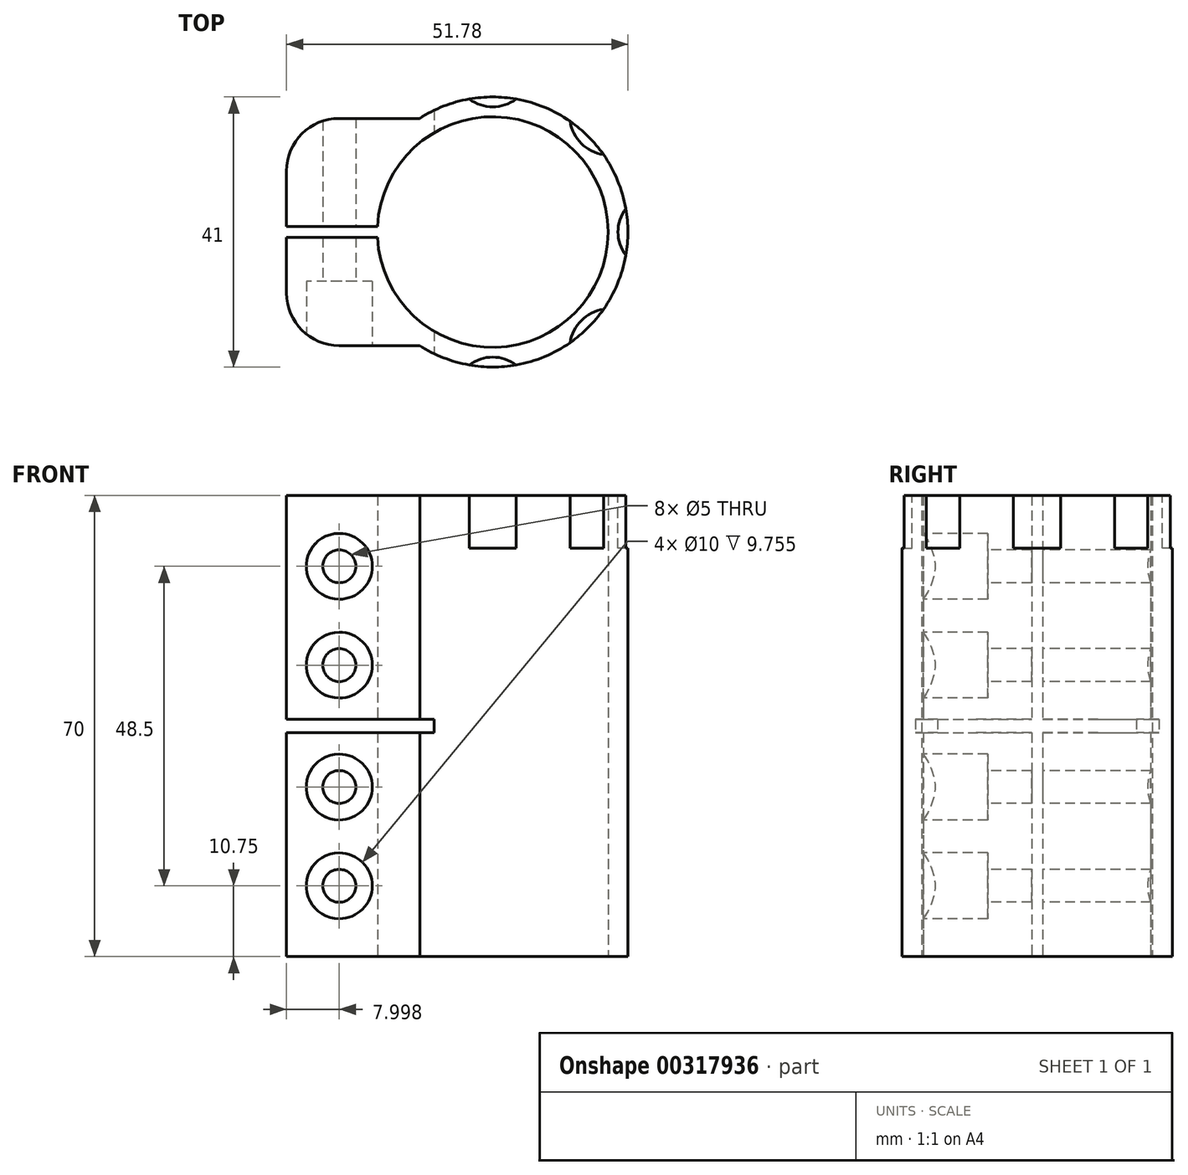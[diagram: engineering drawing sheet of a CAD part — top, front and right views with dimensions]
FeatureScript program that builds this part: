
annotation { "Feature Type Name" : "Feature", "Feature Type Description" : "" }
export const myFeature = defineFeature(function(context is Context, id is Id, definition is map)
    precondition{}
    {
        {
            var Q0;
            Q0=qCreatedBy(makeId("Top.planeOp"),FACE);
            var sketch = newSketch(context, id + "F0", { "sketchPlane" : qUnion([Q0])});
            skArc(sketch, "E0", {"start": v(-17.48, -0.85) * mm, "mid": v(17.5, 0) * mm, "end": v(-17.48, 0.85) * mm});
            skArc(sketch, "E1", {"start": v(-11.08, -17.25) * mm, "mid": v(20.5, 0) * mm, "end": v(-11.08, 17.25) * mm});
            skLineSegment(sketch, "E2", {"start": v(-11.08, 17.25) * mm, "end": v(-23.28, 17.25) * mm});
            skLineSegment(sketch, "E3", {"start": v(-31.28, 9.25) * mm, "end": v(-31.28, 0.85) * mm});
            skLineSegment(sketch, "E4", {"start": v(-31.28, 0.85) * mm, "end": v(-20.48, 0.85) * mm});
            skPoint(sketch, "E5.visualSharp", {"position": v(-31.28, 17.25) * mm});
            skArc(sketch, "E5.filletArc", {"start": v(-23.28, 17.25) * mm, "mid": v(-28.94, 14.9) * mm, "end": v(-31.28, 9.25) * mm});
            skLineSegment(sketch, "E6", {"start": v(0, 0) * mm, "end": v(31.62, 0) * mm, "construction": true});
            skLineSegment(sketch, "E7.MirrorCS", {"start": v(-31.28, -0.85) * mm, "end": v(-20.48, -0.85) * mm});
            skLineSegment(sketch, "E8.MirrorCS", {"start": v(-11.08, -17.25) * mm, "end": v(-23.28, -17.25) * mm});
            skLineSegment(sketch, "E9.MirrorCS", {"start": v(-31.28, -9.25) * mm, "end": v(-31.28, -0.85) * mm});
            skArc(sketch, "E10.MirrorCS", {"start": v(-23.28, -17.25) * mm, "mid": v(-28.94, -14.9) * mm, "end": v(-31.28, -9.25) * mm});
            skLineSegment(sketch, "E11", {"start": v(-20.48, 0.85) * mm, "end": v(-17.48, 0.85) * mm});
            skLineSegment(sketch, "E12", {"start": v(-20.48, -0.85) * mm, "end": v(-17.48, -0.85) * mm});
            skSolve(sketch);
        }
        {
            var Q0;
            Q0=qSketchRegion(id+"F0",true);
            extrude(context, id + "F1", {"entities" : qUnion([Q0]), "endBound" : BoundingType.SYMMETRIC, "depth" : 70 * mm});
        }
        {
            var Q0;
            Q0=makeQuery(id+"F1.opExtrude","SWEPT_FACE",FACE,{"disambiguationData":[OSD([sQuery(id+"F0.wireOp",EDGE,"E8.MirrorCS")])]});
            var sketch = newSketch(context, id + "F2", { "sketchPlane" : qUnion([Q0])});
            skPoint(sketch, "E13", {"position": v(-5.74, 0) * mm});
            skPoint(sketch, "E14", {"position": v(-23.28, -24.25) * mm});
            skPoint(sketch, "E15", {"position": v(-23.28, -9.25) * mm});
            skPoint(sketch, "E16", {"position": v(-23.28, 9.25) * mm});
            skPoint(sketch, "E17", {"position": v(-23.28, 24.25) * mm});
            skSolve(sketch);
        }
        {
            var Q0;
            Q0=sQuery(id+"F2.wireOp",VERTEX,"E14");
            var Q1;
            Q1=sQuery(id+"F2.wireOp",VERTEX,"E15");
            var Q2;
            Q2=sQuery(id+"F2.wireOp",VERTEX,"E16");
            var Q3;
            Q3=sQuery(id+"F2.wireOp",VERTEX,"E17");
            var Q4;
            Q4=makeQuery(id+"F1.opExtrude","SWEPT_BODY",BODY,{"disambiguationData":[OSD([sQuery(id+"F0.wireOp",EDGE,"E0"),sQuery(id+"F0.wireOp",EDGE,"E1"),sQuery(id+"F0.wireOp",EDGE,"E2"),sQuery(id+"F0.wireOp",EDGE,"E3"),sQuery(id+"F0.wireOp",EDGE,"E4"),sQuery(id+"F0.wireOp",EDGE,"E5.filletArc"),sQuery(id+"F0.wireOp",EDGE,"E7.MirrorCS"),sQuery(id+"F0.wireOp",EDGE,"E8.MirrorCS"),sQuery(id+"F0.wireOp",EDGE,"E9.MirrorCS"),sQuery(id+"F0.wireOp",EDGE,"E10.MirrorCS"),sQuery(id+"F0.wireOp",EDGE,"E11"),sQuery(id+"F0.wireOp",EDGE,"E12")])]});
            hole(context, id + "F3", {"style" : HoleStyle.C_BORE, "endStyle" : HoleEndStyle.THROUGH, "holeDiameter" : 5 * mm, "cBoreDiameter" : 10 * mm, "cBoreDepth" : 8 * mm, "locations" : qUnion([Q0, Q1, Q2, Q3]), "scope" : qUnion([Q4]), "isTappedThrough" : true});
        }
        {
            var Q0;
            Q0=makeQuery(id+"F1.opExtrude","SWEPT_FACE",FACE,{"disambiguationData":[OSD([sQuery(id+"F0.wireOp",EDGE,"E8.MirrorCS")])]});
            var sketch = newSketch(context, id + "F4", { "sketchPlane" : qUnion([Q0])});
            skLineSegment(sketch, "E18.bottom", {"start": v(-31.28, 1) * mm, "end": v(-8.88, 1) * mm});
            skLineSegment(sketch, "E18.top", {"start": v(-31.28, -1) * mm, "end": v(-8.88, -1) * mm});
            skLineSegment(sketch, "E18.left", {"start": v(-31.28, 1) * mm, "end": v(-31.28, -1) * mm});
            skLineSegment(sketch, "E18.right", {"start": v(-8.88, 1) * mm, "end": v(-8.88, -1) * mm});
            skSolve(sketch);
        }
        {
            var Q0;
            Q0=qSketchRegion(id+"F4",true);
            extrude(context, id + "F5", {"entities" : qUnion([Q0]), "operationType" : NewBodyOperationType.REMOVE, "endBound" : BoundingType.SYMMETRIC, "oppositeDirection" : true, "depth" : 700 * mm});
        }
        {
            var Q0;
            Q0=makeQuery(id+"F1.opExtrude","CAP_FACE",FACE,{"disambiguationData":[OSD([sQuery(id+"F0.wireOp",EDGE,"E0"),sQuery(id+"F0.wireOp",EDGE,"E1"),sQuery(id+"F0.wireOp",EDGE,"E2"),sQuery(id+"F0.wireOp",EDGE,"E3"),sQuery(id+"F0.wireOp",EDGE,"E4"),sQuery(id+"F0.wireOp",EDGE,"E5.filletArc"),sQuery(id+"F0.wireOp",EDGE,"E7.MirrorCS"),sQuery(id+"F0.wireOp",EDGE,"E8.MirrorCS"),sQuery(id+"F0.wireOp",EDGE,"E9.MirrorCS"),sQuery(id+"F0.wireOp",EDGE,"E10.MirrorCS"),sQuery(id+"F0.wireOp",EDGE,"E11"),sQuery(id+"F0.wireOp",EDGE,"E12")])],"isStart":false});
            var sketch = newSketch(context, id + "F6", { "sketchPlane" : qUnion([Q0])});
            skCircle(sketch, "E19", {"center": v(0, -25) * mm, "radius": 6 * mm});
            skCircle(sketch, "E20.1.0", {"center": v(17.68, -17.68) * mm, "radius": 6 * mm});
            skCircle(sketch, "E20.2.0", {"center": v(25, 0) * mm, "radius": 6 * mm});
            skCircle(sketch, "E20.3.0", {"center": v(17.68, 17.68) * mm, "radius": 6 * mm});
            skCircle(sketch, "E20.4.0", {"center": v(0, 25) * mm, "radius": 6 * mm});
            skPoint(sketch, "E20.center", {"position": v(0, 0) * mm});
            skLineSegment(sketch, "E20.anchor1", {"start": v(0, 0) * mm, "end": v(0, -25) * mm, "construction": true});
            skLineSegment(sketch, "E20.anchor2", {"start": v(0, 0) * mm, "end": v(0, 25) * mm, "construction": true});
            skSolve(sketch);
        }
        {
            var Q0;
            {var subQ0=sQuery(id+"F6.wireOp",EDGE,"E19");var subQ1=makeQuery(id+"F1.opExtrude","CAP_EDGE",EDGE,{"disambiguationData":[OSD([sQuery(id+"F0.wireOp",EDGE,"E1")])],"isStart":false});var subQ2=makeQuery(id+"F6.imprint","INTERSECT",VERTEX,{"disambiguationData":[OD(0.0)],"derivedFrom":[subQ1,subQ0]});Q0=makeQuery(id+"F6.imprint","IMPRINT",FACE,{"disambiguationData":[TD([[makeQuery(id+"F6.imprint","IMPRINT",EDGE,{"disambiguationData":[TD([[subQ2,1.0]])],"derivedFrom":subQ0}),1.0]])]});}
            var Q1;
            {var subQ0=sQuery(id+"F6.wireOp",EDGE,"E20.1.0");var subQ1=makeQuery(id+"F1.opExtrude","CAP_EDGE",EDGE,{"disambiguationData":[OSD([sQuery(id+"F0.wireOp",EDGE,"E1")])],"isStart":false});var subQ2=makeQuery(id+"F6.imprint","INTERSECT",VERTEX,{"disambiguationData":[OD(0.0)],"derivedFrom":[subQ1,subQ0]});Q1=makeQuery(id+"F6.imprint","IMPRINT",FACE,{"disambiguationData":[TD([[makeQuery(id+"F6.imprint","IMPRINT",EDGE,{"disambiguationData":[TD([[subQ2,1.0]])],"derivedFrom":subQ0}),1.0]])]});}
            var Q2;
            {var subQ0=sQuery(id+"F6.wireOp",EDGE,"E20.2.0");var subQ1=makeQuery(id+"F1.opExtrude","CAP_EDGE",EDGE,{"disambiguationData":[OSD([sQuery(id+"F0.wireOp",EDGE,"E1")])],"isStart":false});var subQ2=makeQuery(id+"F6.imprint","INTERSECT",VERTEX,{"disambiguationData":[OD(0.0)],"derivedFrom":[subQ1,subQ0]});Q2=makeQuery(id+"F6.imprint","IMPRINT",FACE,{"disambiguationData":[TD([[makeQuery(id+"F6.imprint","IMPRINT",EDGE,{"disambiguationData":[TD([[subQ2,1.0]])],"derivedFrom":subQ0}),1.0]])]});}
            var Q3;
            {var subQ0=sQuery(id+"F6.wireOp",EDGE,"E20.3.0");var subQ1=makeQuery(id+"F1.opExtrude","CAP_EDGE",EDGE,{"disambiguationData":[OSD([sQuery(id+"F0.wireOp",EDGE,"E1")])],"isStart":false});var subQ2=makeQuery(id+"F6.imprint","INTERSECT",VERTEX,{"disambiguationData":[OD(0.0)],"derivedFrom":[subQ1,subQ0]});Q3=makeQuery(id+"F6.imprint","IMPRINT",FACE,{"disambiguationData":[TD([[makeQuery(id+"F6.imprint","IMPRINT",EDGE,{"disambiguationData":[TD([[subQ2,-1.0]])],"derivedFrom":subQ0}),1.0]])]});}
            var Q4;
            {var subQ0=sQuery(id+"F6.wireOp",EDGE,"E20.4.0");var subQ1=makeQuery(id+"F1.opExtrude","CAP_EDGE",EDGE,{"disambiguationData":[OSD([sQuery(id+"F0.wireOp",EDGE,"E1")])],"isStart":false});var subQ2=makeQuery(id+"F6.imprint","INTERSECT",VERTEX,{"disambiguationData":[OD(0.0)],"derivedFrom":[subQ1,subQ0]});Q4=makeQuery(id+"F6.imprint","IMPRINT",FACE,{"disambiguationData":[TD([[makeQuery(id+"F6.imprint","IMPRINT",EDGE,{"disambiguationData":[TD([[subQ2,-1.0]])],"derivedFrom":subQ0}),1.0]])]});}
            extrude(context, id + "F7", {"entities" : qUnion([Q0, Q1, Q2, Q3, Q4]), "operationType" : NewBodyOperationType.REMOVE, "oppositeDirection" : true, "depth" : 8 * mm});
        }
    });
